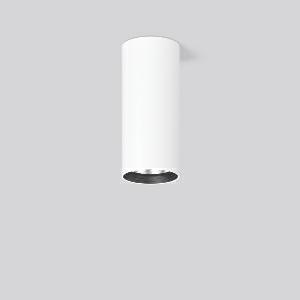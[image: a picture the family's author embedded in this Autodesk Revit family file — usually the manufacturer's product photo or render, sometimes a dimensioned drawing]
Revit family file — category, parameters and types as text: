
# Revit family: heledon_mini_a_931210_002_1_76_9c35
name_source: partatom
category: Lighting Fixtures
units: mm (PartAtom-declared; Revit-internal decimal feet)

## family parameters
Cut with Voids When Loaded = No
Host = Face
Light Source = No
Part Type = Normal
Room Calculation Point = No
Round Connector Dimension = Use Diameter
Shared = No

## types (1)
- HELEDON mini A (1 x LED Modul 940, 3900 lm, 4000)
    Apparent Load = 29 VA
    Approval mark = CE
    CIE Flux Codes = 95 99 100 100 100
    Color Rendering = 92
    Color Temperature = 4000
    Default Elevation = 1800 mm
    Description = Series: HELEDON mini
Cylindrical surface-mounted downlight. Housing: die-cast aluminium, powder-coated. Internal ceiling frame polycarbonate with bayonet mounting. Black plastic ring and recessed LED to prevent glare from the side. Optical assembly with reflector made of MIRO-Silver with 98% total light reflection for outstanding efficiency - can be changed without tools. Best colour rendering index Ra>90. Suitable for Ceiling mounting. Easy installation with a separate ceiling frame with bayonet mounting and plug connection. Driver integrated. Connected via plug-in connector. High quality converter without flickering and stroboscopic effect. The following accessories can be mounted without use of tools: interchangeable lenses, decorative glasses, honeycomb louvre, clear and frosted diffusers, white interchangeable plastic ring. 
Colour: traffic white, matt (RAL 9016)
Diameter: 87 mm
Height: 197 mm
Lamp: LED
Socket: without socket
Colour temperature: 4000K
Colour rendering index (CRI): 92
System power: 29 W
Rated luminous flux: 3900 lm
Luminous efficiency: 134 lm/W
Control gear: Converter, dimmable, DALI
Protection class: I
Type of protection: IP 20
    Height = 197 mm
    Lamp = 1 x LED Modul 940
    Lamp Light Flux = 3900 lm
    Lamp count = 1
    Length = 87 mm
    Lifetime = 50000 h
    Luminous efficacy = 134 lm/W
    Manufacturer = RZB
    ModVariant = No
    Model = 931210.002.1.76
    Mounting Place = Ceiling
    Mounting Type = Surface mounted
    Number of Poles = 1
    OnlyDefault = Yes
    Power Factor = 1
    Product Name = HELEDON mini A
    Product group = Surface mounted downlights
    ProductGroupID = 302
    Protection Class = Protection class I
    Protection Degree = IP 20
    RLX_Detail_Level = 1
    RLX_Emergency_Light_Flux = 0 lm
    RLX_Emergency_Type = 0
    RLX_Emergency_Type_DB = No
    RlxData = <blob elided: 107061 chars, md5=4785cf07>
    Socket = socket
    Standby Power = 0 W
    System Light Flux = 3900 lm
    System Power = 29 W
    Type Comments = Product without accessories
    Type Image = 931188.002.jpg
    URL = http://relux.com
    VarID = ---
    Voltage = 230 V
    Voltage Range = 220-240 V
    Weight = 0.00 kg
    Width = 0 mm  [stored 0 ft]

note: [stored X ft] marks values corroborated as IEEE doubles in the binary element streams (Revit-internal decimal feet)

## geometry (parser evidence)
native form markers: Blend x4, Sweep x10
no freeform markers — native parametric forms only
